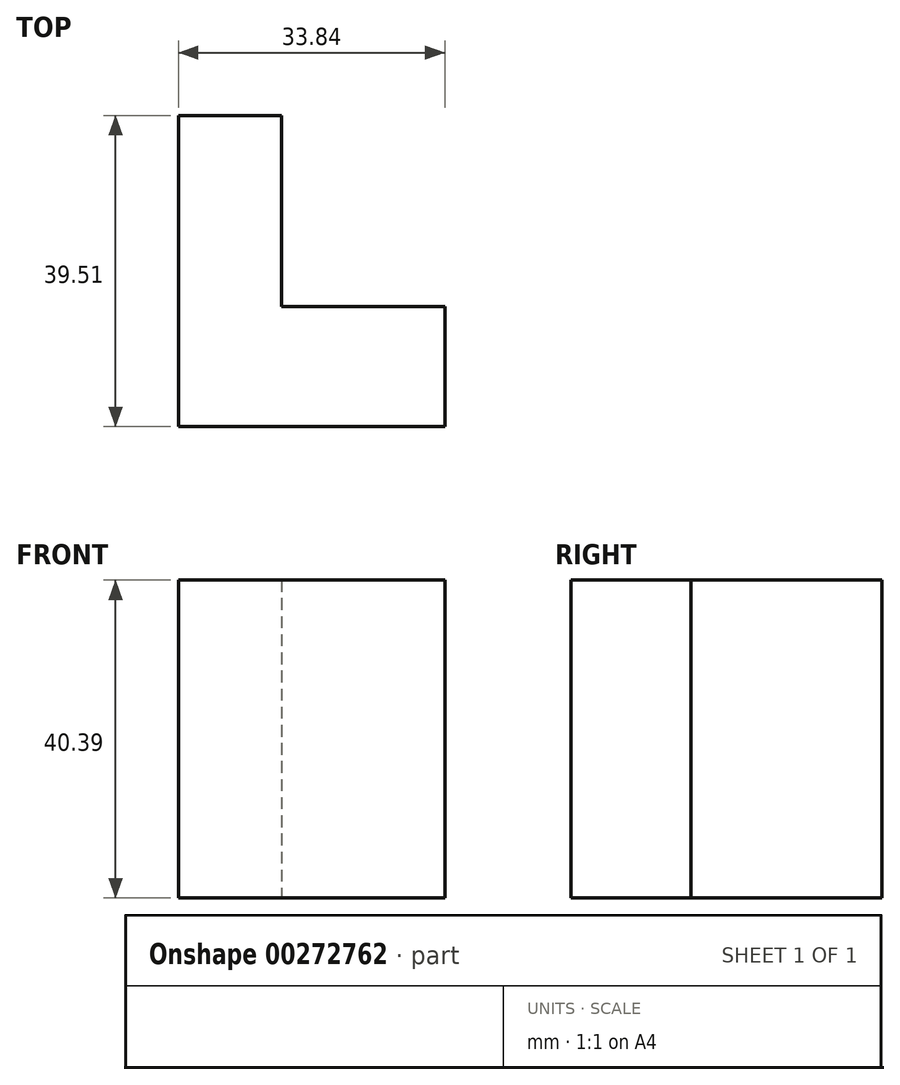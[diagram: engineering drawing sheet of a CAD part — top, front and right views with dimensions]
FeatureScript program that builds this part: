
annotation { "Feature Type Name" : "Feature", "Feature Type Description" : "" }
export const myFeature = defineFeature(function(context is Context, id is Id, definition is map)
    precondition{}
    {
        {
            var Q0;
            Q0=qCreatedBy(makeId("Top.planeOp"),FACE);
            var sketch = newSketch(context, id + "F0", { "sketchPlane" : qUnion([Q0])});
            skLineSegment(sketch, "E0", {"start": v(-23.08, 43.62) * mm, "end": v(-23.08, 4.1) * mm});
            skLineSegment(sketch, "E1", {"start": v(-23.08, 4.1) * mm, "end": v(10.76, 4.1) * mm});
            skLineSegment(sketch, "E2", {"start": v(10.76, 4.1) * mm, "end": v(10.76, 19.37) * mm});
            skLineSegment(sketch, "E3", {"start": v(10.76, 19.37) * mm, "end": v(-9.98, 19.37) * mm});
            skLineSegment(sketch, "E4", {"start": v(-9.98, 19.37) * mm, "end": v(-9.98, 43.62) * mm});
            skLineSegment(sketch, "E5", {"start": v(-9.98, 43.62) * mm, "end": v(-23.08, 43.62) * mm});
            skSolve(sketch);
        }
        {
            var Q0;
            Q0 = qSketchRegion(id + "F0", true);
            extrude(context, id + "F1", {"entities" : qUnion([Q0]), "depth" : 40.4 * mm});
        }
    });
